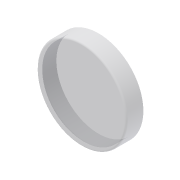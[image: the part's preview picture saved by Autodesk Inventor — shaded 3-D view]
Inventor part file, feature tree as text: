
AUTODESK INVENTOR PART (.ipt)
format: ipt  version: 2014 (Build 180170000, 170)  size: 115,200 bytes
history: native  units: mm
features: extrude x2, sketch x2, fillet x1
ambient origin geometry x8: Origin, YZ Plane, XZ Plane, XY Plane, X Axis, Y Axis, Z Axis, Center Point
bodies: Solid1 (feature_tree)
feature tree (5):
  extrude  "Extrusion1"  Depth=2.0mm TaperAngle=0.0deg
  extrude  "Extrusion2"  Depth=2.0mm
  fillet  "Fillet1"  Radius=100.0mm
  sketch  "Sketch1"  dims[d0=100.0mm d1=2.0mm d2=0.0mm]
  sketch  "Sketch2"  dims[d5=17.0mm d6=0.0mm d7=2.0mm d8=100.0mm d9=3.0mm]
